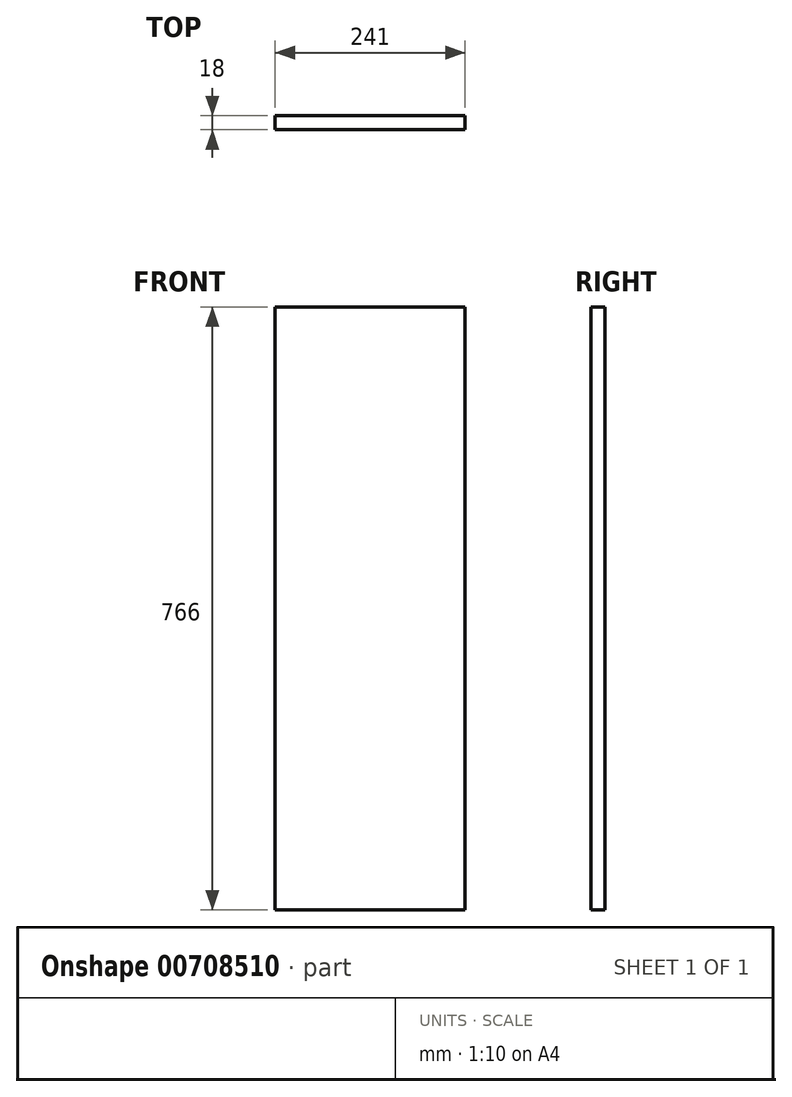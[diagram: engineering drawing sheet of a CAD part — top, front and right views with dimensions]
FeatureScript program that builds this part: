
annotation { "Feature Type Name" : "Feature", "Feature Type Description" : "" }
export const myFeature = defineFeature(function(context is Context, id is Id, definition is map)
    precondition{}
    {
        {
            var Q0;
            Q0=qCreatedBy(makeId("Front.planeOp"),FACE);
            var sketch = newSketch(context, id + "F0", { "sketchPlane" : qUnion([Q0])});
            skLineSegment(sketch, "E0.bottom", {"start": v(0, 0) * mm, "end": v(-241, 0) * mm});
            skLineSegment(sketch, "E0.top", {"start": v(0, -766) * mm, "end": v(-241, -766) * mm});
            skLineSegment(sketch, "E0.left", {"start": v(0, 0) * mm, "end": v(0, -766) * mm});
            skLineSegment(sketch, "E0.right", {"start": v(-241, 0) * mm, "end": v(-241, -766) * mm});
            skSolve(sketch);
        }
        {
            var Q0;
            Q0=qSketchRegion(id+"F0",true);
            extrude(context, id + "F1", {"entities" : qUnion([Q0]), "depth" : 18 * mm, "offsetDistance" : 25 * mm});
        }
    });
